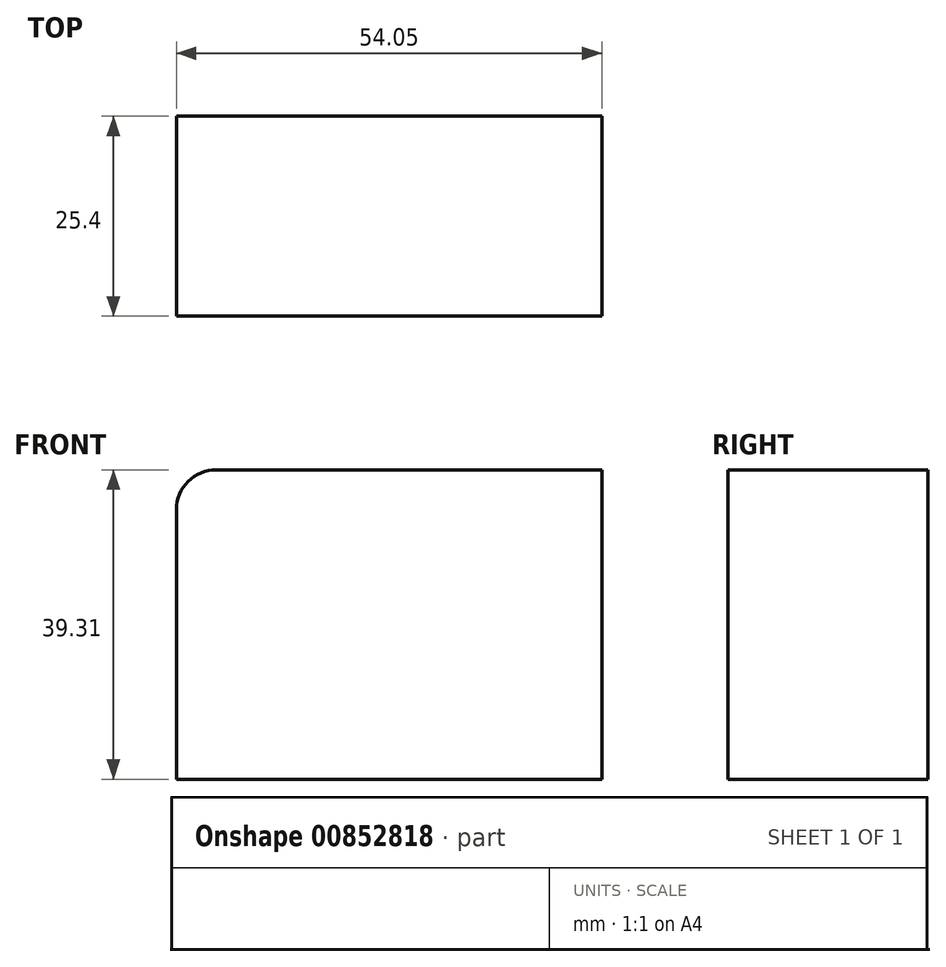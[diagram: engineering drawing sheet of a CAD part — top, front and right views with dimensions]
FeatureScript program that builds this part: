
annotation { "Feature Type Name" : "Feature", "Feature Type Description" : "" }
export const myFeature = defineFeature(function(context is Context, id is Id, definition is map)
    precondition{}
    {
        {
            var Q0;
            Q0=qCreatedBy(makeId("Front.planeOp"),FACE);
            var sketch = newSketch(context, id + "F0", { "sketchPlane" : qUnion([Q0])});
            skLineSegment(sketch, "E0.bottom", {"start": v(-106.79, 54.02) * mm, "end": v(-52.74, 54.02) * mm});
            skLineSegment(sketch, "E0.top", {"start": v(-106.79, 14.7) * mm, "end": v(-52.74, 14.7) * mm});
            skLineSegment(sketch, "E0.left", {"start": v(-106.79, 54.02) * mm, "end": v(-106.79, 14.7) * mm});
            skLineSegment(sketch, "E0.right", {"start": v(-52.74, 54.02) * mm, "end": v(-52.74, 14.7) * mm});
            skSolve(sketch);
        }
        {
            var Q0;
            Q0 = qSketchRegion(id + "F0", true);
            extrude(context, id + "F1", {"entities" : qUnion([Q0]), "depth" : 25.4 * mm, "offsetDistance" : 25.4 * mm});
        }
        {
            var Q0;
            Q0=makeQuery(id+"F1.opExtrude","SWEPT_EDGE",EDGE,{"disambiguationData":[OSD([sQuery(id+"F0.wireOp",EDGE,"E0.bottom"),sQuery(id+"F0.wireOp",EDGE,"E0.left")])]});
            fillet(context, id + "F2", {"entities" : qUnion([Q0]), "radius" : 5.08 * mm, "tangentPropagation" : true, "allowEdgeOverflow" : false});
        }
    });
